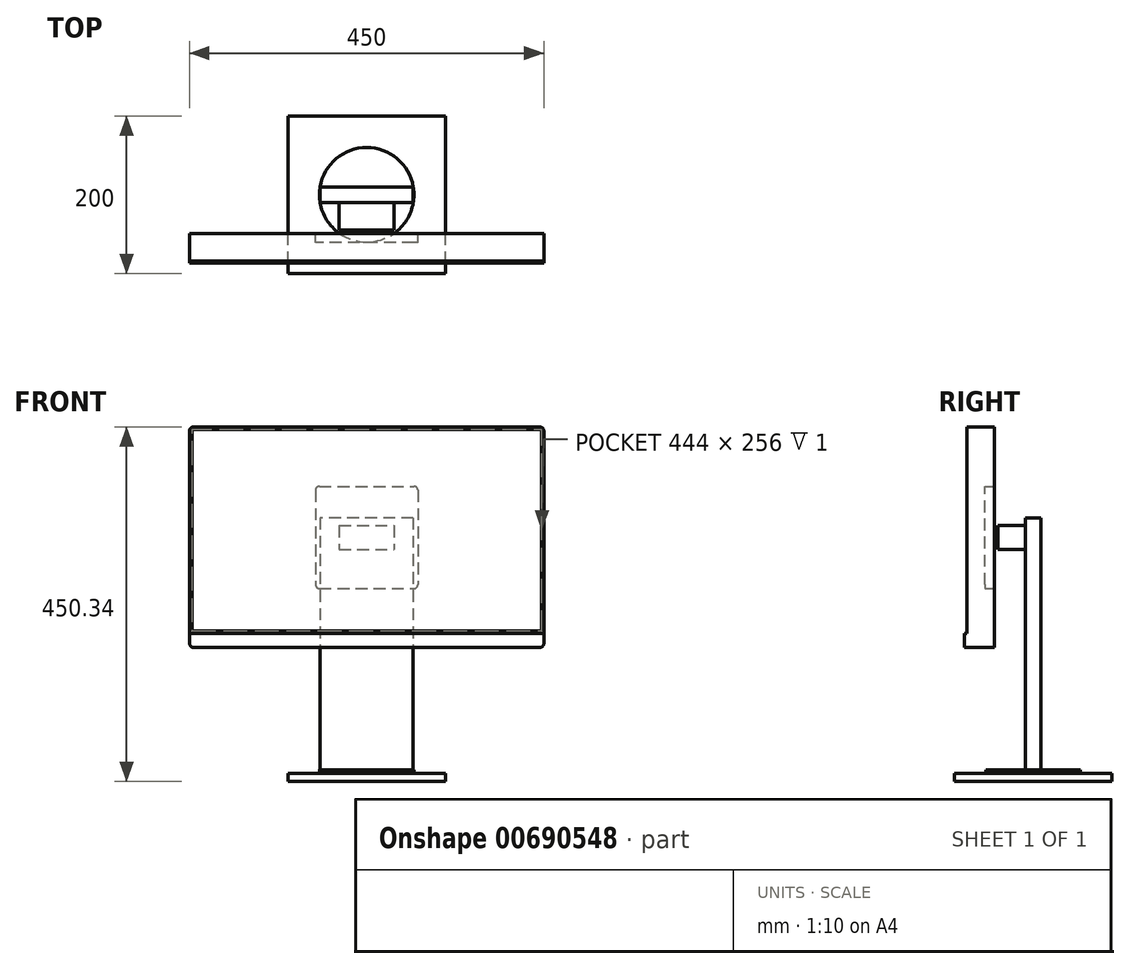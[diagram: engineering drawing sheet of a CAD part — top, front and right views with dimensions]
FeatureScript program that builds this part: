
annotation { "Feature Type Name" : "Feature", "Feature Type Description" : "" }
export const myFeature = defineFeature(function(context is Context, id is Id, definition is map)
    precondition{}
    {
        {
            var Q0;
            Q0=qCreatedBy(makeId("Top.planeOp"),FACE);
            var sketch = newSketch(context, id + "F0", { "sketchPlane" : qUnion([Q0])});
            skLineSegment(sketch, "E0.bottom", {"start": v(-100, -100) * mm, "end": v(100, -100) * mm});
            skLineSegment(sketch, "E0.top", {"start": v(-100, 100) * mm, "end": v(100, 100) * mm});
            skLineSegment(sketch, "E0.left", {"start": v(-100, -100) * mm, "end": v(-100, 100) * mm});
            skLineSegment(sketch, "E0.right", {"start": v(100, -100) * mm, "end": v(100, 100) * mm});
            skPoint(sketch, "E0.middle", {"position": v(0, 0) * mm});
            skSolve(sketch);
        }
        {
            var Q0;
            Q0 = qSketchRegion(id + "F0", true);
            extrude(context, id + "F1", {"entities" : qUnion([Q0]), "depth" : 10 * mm, "offsetDistance" : 25 * mm});
        }
        {
            var Q0;
            Q0=makeQuery(id+"F1.opExtrude","CAP_FACE",FACE,{"disambiguationData":[OSD([sQuery(id+"F0.wireOp",EDGE,"E0.bottom"),sQuery(id+"F0.wireOp",EDGE,"E0.top"),sQuery(id+"F0.wireOp",EDGE,"E0.left"),sQuery(id+"F0.wireOp",EDGE,"E0.right")])],"isStart":false});
            var sketch = newSketch(context, id + "F2", { "sketchPlane" : qUnion([Q0])});
            skCircle(sketch, "E1", {"center": v(0, 0) * mm, "radius": 60 * mm});
            skSolve(sketch);
        }
        {
            var Q0;
            Q0 = qSketchRegion(id + "F2", true);
            extrude(context, id + "F3", {"entities" : qUnion([Q0]), "operationType" : NewBodyOperationType.ADD, "depth" : 5 * mm, "offsetDistance" : 25 * mm});
        }
        {
            var Q0;
            Q0=makeQuery(id+"F3.opExtrude","CAP_FACE",FACE,{"disambiguationData":[OSD([sQuery(id+"F2.wireOp",EDGE,"E1")])],"isStart":false});
            var sketch = newSketch(context, id + "F4", { "sketchPlane" : qUnion([Q0])});
            skLineSegment(sketch, "E2.bottom", {"start": v(59.16, -10) * mm, "end": v(-59.16, -10) * mm});
            skLineSegment(sketch, "E2.top", {"start": v(59.16, 10) * mm, "end": v(-59.16, 10) * mm});
            skLineSegment(sketch, "E2.left", {"start": v(59.16, -10) * mm, "end": v(59.16, 10) * mm});
            skLineSegment(sketch, "E2.right", {"start": v(-59.16, -10) * mm, "end": v(-59.16, 10) * mm});
            skPoint(sketch, "E2.middle", {"position": v(0, 0) * mm});
            skSolve(sketch);
        }
        {
            var Q0;
            Q0=makeQuery(id+"F4.imprint","IMPRINT",FACE,{"disambiguationData":[TD([[makeQuery(id+"F4.imprint","IMPRINT",EDGE,{"derivedFrom":sQuery(id+"F4.wireOp",EDGE,"E2.bottom")}),-1.0]])]});
            extrude(context, id + "F5", {"entities" : qUnion([Q0]), "operationType" : NewBodyOperationType.ADD, "depth" : 320 * mm, "offsetDistance" : 25 * mm});
        }
        {
            var Q0;
            Q0=makeQuery(id+"F5.opExtrude","SWEPT_FACE",FACE,{"disambiguationData":[OSD([sQuery(id+"F4.wireOp",EDGE,"E2.bottom")])]});
            var sketch = newSketch(context, id + "F6", { "sketchPlane" : qUnion([Q0])});
            skLineSegment(sketch, "E3.bottom", {"start": v(-35, 325) * mm, "end": v(35, 325) * mm});
            skLineSegment(sketch, "E3.top", {"start": v(-35, 295) * mm, "end": v(35, 295) * mm});
            skLineSegment(sketch, "E3.left", {"start": v(-35, 325) * mm, "end": v(-35, 295) * mm});
            skLineSegment(sketch, "E3.right", {"start": v(35, 325) * mm, "end": v(35, 295) * mm});
            skPoint(sketch, "E4", {"position": v(0, 325) * mm});
            skPoint(sketch, "E5", {"position": v(0, 335) * mm});
            skSolve(sketch);
        }
        {
            var Q0;
            Q0=makeQuery(id+"F6.imprint","IMPRINT",FACE,{"disambiguationData":[TD([[makeQuery(id+"F6.imprint","IMPRINT",EDGE,{"derivedFrom":sQuery(id+"F6.wireOp",EDGE,"E3.bottom")}),-1.0]])]});
            extrude(context, id + "F7", {"entities" : qUnion([Q0]), "operationType" : NewBodyOperationType.ADD, "depth" : 35 * mm, "offsetDistance" : 25 * mm});
        }
        {
            var Q0;
            Q0=makeQuery(id+"F7.opExtrude","CAP_FACE",FACE,{"disambiguationData":[OSD([sQuery(id+"F6.wireOp",EDGE,"E3.bottom"),sQuery(id+"F6.wireOp",EDGE,"E3.top"),sQuery(id+"F6.wireOp",EDGE,"E3.left"),sQuery(id+"F6.wireOp",EDGE,"E3.right")])],"isStart":false});
            var sketch = newSketch(context, id + "F8", { "sketchPlane" : qUnion([Q0])});
            skPoint(sketch, "E6", {"position": v(0, 310) * mm});
            skPoint(sketch, "E7", {"position": v(-35, 310) * mm});
            skLineSegment(sketch, "E8.bottom", {"start": v(60, 245) * mm, "end": v(-60, 245) * mm});
            skLineSegment(sketch, "E8.top", {"start": v(60, 375) * mm, "end": v(-60, 375) * mm});
            skLineSegment(sketch, "E8.left", {"start": v(65, 250) * mm, "end": v(65, 370) * mm});
            skLineSegment(sketch, "E8.right", {"start": v(-65, 250) * mm, "end": v(-65, 370) * mm});
            skPoint(sketch, "E9.visualSharp", {"position": v(-65, 375) * mm});
            skArc(sketch, "E9.filletArc", {"start": v(-60, 375) * mm, "mid": v(-63.54, 373.54) * mm, "end": v(-65, 370) * mm});
            skPoint(sketch, "E10.visualSharp", {"position": v(65, 375) * mm});
            skArc(sketch, "E10.filletArc", {"start": v(65, 370) * mm, "mid": v(63.54, 373.54) * mm, "end": v(60, 375) * mm});
            skPoint(sketch, "E11.visualSharp", {"position": v(65, 245) * mm});
            skArc(sketch, "E11.filletArc", {"start": v(60, 245) * mm, "mid": v(63.54, 246.46) * mm, "end": v(65, 250) * mm});
            skPoint(sketch, "E12.visualSharp", {"position": v(-65, 245) * mm});
            skArc(sketch, "E12.filletArc", {"start": v(-65, 250) * mm, "mid": v(-63.54, 246.46) * mm, "end": v(-60, 245) * mm});
            skSolve(sketch);
        }
        {
            var Q0;
            Q0 = qSketchRegion(id + "F8", true);
            extrude(context, id + "F9", {"entities" : qUnion([Q0]), "operationType" : NewBodyOperationType.ADD, "depth" : 4 * mm, "offsetDistance" : 25 * mm});
        }
        {
            var Q0;
            Q0=makeQuery(id+"F9.opExtrude","CAP_FACE",FACE,{"disambiguationData":[OSD([sQuery(id+"F8.wireOp",EDGE,"E8.bottom"),sQuery(id+"F8.wireOp",EDGE,"E8.top"),sQuery(id+"F8.wireOp",EDGE,"E8.left"),sQuery(id+"F8.wireOp",EDGE,"E8.right"),sQuery(id+"F8.wireOp",EDGE,"E9.filletArc"),sQuery(id+"F8.wireOp",EDGE,"E10.filletArc"),sQuery(id+"F8.wireOp",EDGE,"E11.filletArc"),sQuery(id+"F8.wireOp",EDGE,"E12.filletArc")])],"isStart":false});
            var sketch = newSketch(context, id + "F10", { "sketchPlane" : qUnion([Q0])});
            skLineSegment(sketch, "E13.bottom", {"start": v(-220, 170.34) * mm, "end": v(220, 170.34) * mm});
            skLineSegment(sketch, "E13.top", {"start": v(-220, 450.34) * mm, "end": v(220, 450.34) * mm});
            skLineSegment(sketch, "E13.left", {"start": v(-225, 175.34) * mm, "end": v(-225, 445.34) * mm});
            skLineSegment(sketch, "E13.right", {"start": v(225, 175.34) * mm, "end": v(225, 445.34) * mm});
            skPoint(sketch, "E13.middle", {"position": v(0, 310.34) * mm});
            skPoint(sketch, "E14.visualSharp", {"position": v(-225, 450.34) * mm});
            skArc(sketch, "E14.filletArc", {"start": v(-220, 450.34) * mm, "mid": v(-223.54, 448.88) * mm, "end": v(-225, 445.34) * mm});
            skPoint(sketch, "E15.visualSharp", {"position": v(225, 450.34) * mm});
            skArc(sketch, "E15.filletArc", {"start": v(225, 445.34) * mm, "mid": v(223.54, 448.88) * mm, "end": v(220, 450.34) * mm});
            skPoint(sketch, "E16.visualSharp", {"position": v(225, 170.34) * mm});
            skArc(sketch, "E16.filletArc", {"start": v(220, 170.34) * mm, "mid": v(223.54, 171.8) * mm, "end": v(225, 175.34) * mm});
            skPoint(sketch, "E17.visualSharp", {"position": v(-225, 170.34) * mm});
            skArc(sketch, "E17.filletArc", {"start": v(-225, 175.34) * mm, "mid": v(-223.54, 171.8) * mm, "end": v(-220, 170.34) * mm});
            skSolve(sketch);
        }
        {
            var Q0;
            Q0 = qSketchRegion(id + "F10", true);
            extrude(context, id + "F11", {"entities" : qUnion([Q0]), "depth" : 35 * mm, "offsetDistance" : 25 * mm});
        }
        {
            var Q0;
            Q0=makeQuery(id+"F8.imprint","IMPRINT",FACE,{"disambiguationData":[TD([[makeQuery(id+"F8.imprint","IMPRINT",EDGE,{"derivedFrom":sQuery(id+"F8.wireOp",EDGE,"E8.bottom")}),-1.0]])]});
            var Q1;
            Q1=makeQuery(id+"F8.imprint","IMPRINT",FACE,{"disambiguationData":[TD([[makeQuery(id+"F8.imprint","IMPRINT",EDGE,{"derivedFrom":makeQuery(id+"F7.opExtrude","CAP_EDGE",EDGE,{"disambiguationData":[OSD([sQuery(id+"F6.wireOp",EDGE,"E3.bottom")])],"isStart":false})}),-1.0]])]});
            extrude(context, id + "F12", {"entities" : qUnion([Q0, Q1]), "operationType" : NewBodyOperationType.REMOVE, "depth" : 16 * mm, "offsetDistance" : 25 * mm});
        }
        {
            var Q0;
            Q0=makeQuery(id+"F11.opExtrude","CAP_FACE",FACE,{"disambiguationData":[OSD([sQuery(id+"F10.wireOp",EDGE,"E13.bottom"),sQuery(id+"F10.wireOp",EDGE,"E13.top"),sQuery(id+"F10.wireOp",EDGE,"E13.left"),sQuery(id+"F10.wireOp",EDGE,"E13.right"),sQuery(id+"F10.wireOp",EDGE,"E14.filletArc"),sQuery(id+"F10.wireOp",EDGE,"E15.filletArc"),sQuery(id+"F10.wireOp",EDGE,"E16.filletArc"),sQuery(id+"F10.wireOp",EDGE,"E17.filletArc")])],"isStart":false});
            var sketch = newSketch(context, id + "F13", { "sketchPlane" : qUnion([Q0])});
            skLineSegment(sketch, "E18.0", {"start": v(-225, 188.34) * mm, "end": v(225, 188.34) * mm});
            skSolve(sketch);
        }
        {
            var Q0;
            {var subQ2=sQuery(id+"F13.wireOp",EDGE,"E18.0");Q0=makeQuery(id+"F13.imprint","IMPRINT",FACE,{"disambiguationData":[TD([[makeQuery(id+"F13.imprint","IMPRINT",EDGE,{"derivedFrom":subQ2}),-1.0]])]});}
            extrude(context, id + "F14", {"entities" : qUnion([Q0]), "operationType" : NewBodyOperationType.ADD, "depth" : 3 * mm, "offsetDistance" : 25 * mm});
        }
        {
            var Q0;
            Q0=makeQuery(id+"F11.opExtrude","CAP_FACE",FACE,{"disambiguationData":[OSD([sQuery(id+"F10.wireOp",EDGE,"E13.bottom"),sQuery(id+"F10.wireOp",EDGE,"E13.top"),sQuery(id+"F10.wireOp",EDGE,"E13.left"),sQuery(id+"F10.wireOp",EDGE,"E13.right"),sQuery(id+"F10.wireOp",EDGE,"E14.filletArc"),sQuery(id+"F10.wireOp",EDGE,"E15.filletArc"),sQuery(id+"F10.wireOp",EDGE,"E16.filletArc"),sQuery(id+"F10.wireOp",EDGE,"E17.filletArc")])],"isStart":false});
            var sketch = newSketch(context, id + "F15", { "sketchPlane" : qUnion([Q0])});
            skLineSegment(sketch, "E19.0", {"start": v(-222, 447.34) * mm, "end": v(222, 447.34) * mm});
            skLineSegment(sketch, "E19.1", {"start": v(-222, 191.34) * mm, "end": v(-222, 447.34) * mm});
            skLineSegment(sketch, "E19.2", {"start": v(-222, 191.34) * mm, "end": v(222, 191.34) * mm});
            skLineSegment(sketch, "E19.3", {"start": v(222, 191.34) * mm, "end": v(222, 447.34) * mm});
            skSolve(sketch);
        }
        {
            var Q0;
            Q0=makeQuery(id+"F15.imprint","IMPRINT",FACE,{"disambiguationData":[TD([[makeQuery(id+"F15.imprint","IMPRINT",EDGE,{"derivedFrom":sQuery(id+"F15.wireOp",EDGE,"E19.0")}),-1.0]])]});
            extrude(context, id + "F16", {"entities" : qUnion([Q0]), "operationType" : NewBodyOperationType.REMOVE, "oppositeDirection" : true, "depth" : 1 * mm, "offsetDistance" : 25 * mm});
        }
    });
